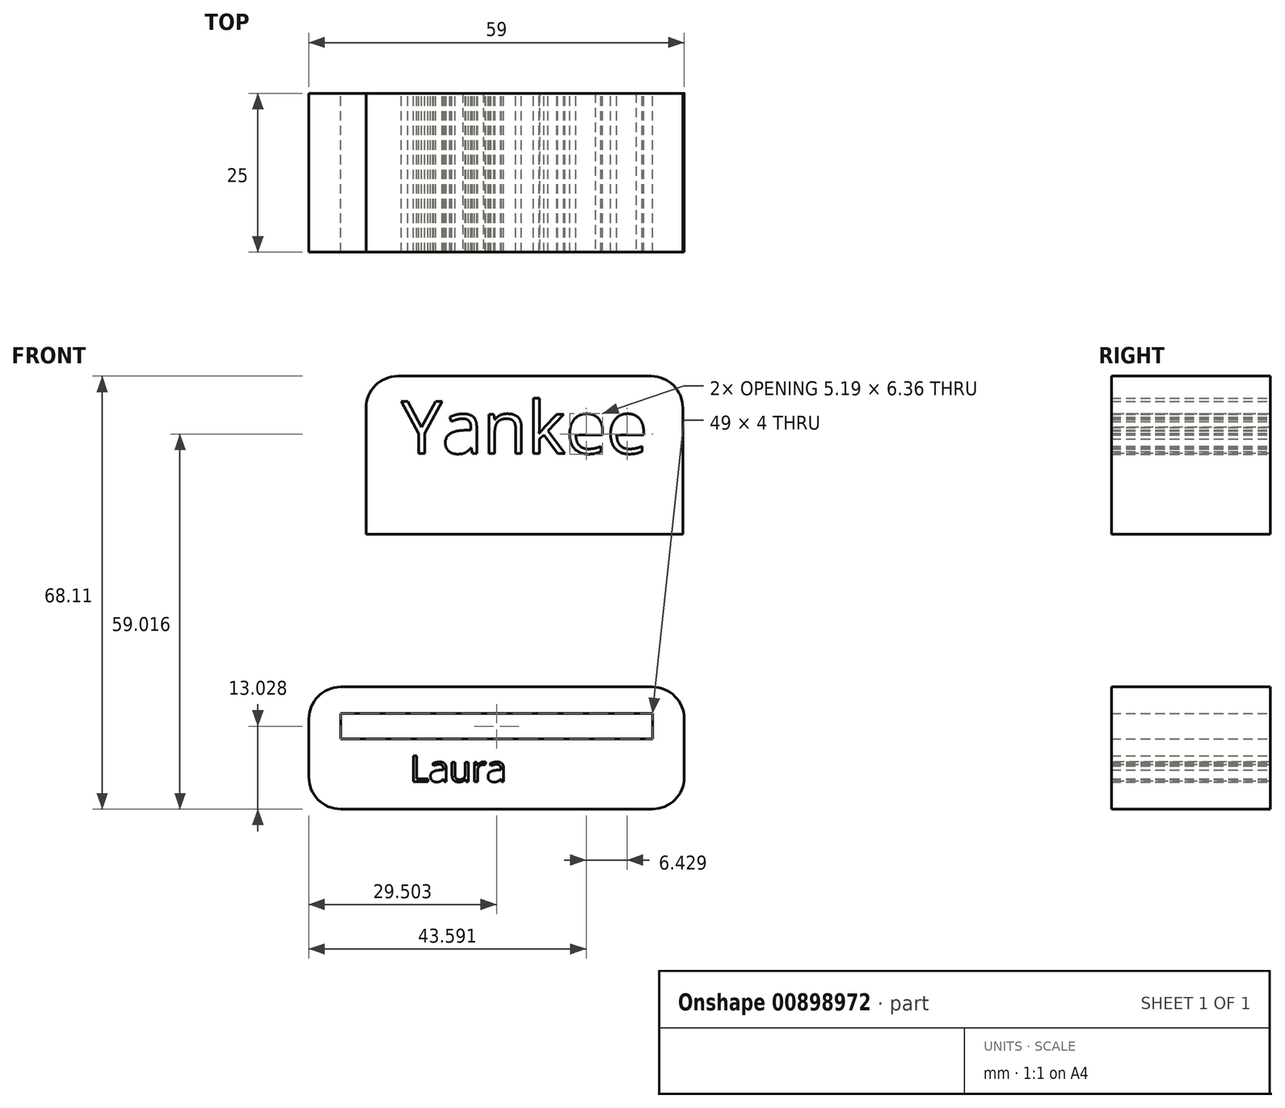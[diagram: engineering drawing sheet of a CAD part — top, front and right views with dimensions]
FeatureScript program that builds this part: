
annotation { "Feature Type Name" : "Feature", "Feature Type Description" : "" }
export const myFeature = defineFeature(function(context is Context, id is Id, definition is map)
    precondition{}
    {
        {
            var Q0;
            Q0=qCreatedBy(makeId("Front.planeOp"),FACE);
            var sketch = newSketch(context, id + "F0", { "sketchPlane" : qUnion([Q0])});
            skLineSegment(sketch, "E0.bottom", {"start": v(-11.79, -18.06) * mm, "end": v(28.01, -18.06) * mm});
            skLineSegment(sketch, "E0.top", {"start": v(-16.79, -42.95) * mm, "end": v(33.01, -42.95) * mm});
            skLineSegment(sketch, "E0.left", {"start": v(-16.79, -23.06) * mm, "end": v(-16.79, -42.95) * mm});
            skLineSegment(sketch, "E0.right", {"start": v(33.01, -23.06) * mm, "end": v(33.01, -42.95) * mm});
            skText(sketch, "E1", { "text": "Yankee\n", "fontName": "OpenSans-Regular.ttf"});
            skPoint(sketch, "E2.2.internal.snap0", {"position": v(8.11, -18.06) * mm});
            skLineSegment(sketch, "E3.bottom", {"start": v(-20.77, -86.17) * mm, "end": v(28.23, -86.17) * mm});
            skLineSegment(sketch, "E3.top", {"start": v(-20.77, -66.97) * mm, "end": v(28.23, -66.97) * mm});
            skLineSegment(sketch, "E3.left", {"start": v(-25.77, -81.17) * mm, "end": v(-25.77, -71.97) * mm});
            skLineSegment(sketch, "E3.right", {"start": v(33.23, -81.17) * mm, "end": v(33.23, -71.97) * mm});
            skPoint(sketch, "E2.2.internal.orphan", {"position": v(8.11, -10.25) * mm});
            skPoint(sketch, "E2.3.internal.orphan", {"position": v(8.16, -8.67) * mm});
            skLineSegment(sketch, "E4.bottom", {"start": v(-20.77, -71.14) * mm, "end": v(28.23, -71.14) * mm});
            skLineSegment(sketch, "E4.top", {"start": v(-20.77, -75.14) * mm, "end": v(28.23, -75.14) * mm});
            skLineSegment(sketch, "E4.left", {"start": v(-20.77, -71.14) * mm, "end": v(-20.77, -75.14) * mm});
            skLineSegment(sketch, "E4.right", {"start": v(28.23, -71.14) * mm, "end": v(28.23, -75.14) * mm});
            skPoint(sketch, "E5.visualSharp", {"position": v(-25.77, -66.97) * mm});
            skArc(sketch, "E5.filletArc", {"start": v(-20.77, -66.97) * mm, "mid": v(-24.3, -68.43) * mm, "end": v(-25.77, -71.97) * mm});
            skPoint(sketch, "E6.visualSharp", {"position": v(33.23, -66.97) * mm});
            skArc(sketch, "E6.filletArc", {"start": v(33.23, -71.97) * mm, "mid": v(31.77, -68.43) * mm, "end": v(28.23, -66.97) * mm});
            skPoint(sketch, "E7.visualSharp", {"position": v(33.23, -86.17) * mm});
            skArc(sketch, "E7.filletArc", {"start": v(28.23, -86.17) * mm, "mid": v(31.77, -84.7) * mm, "end": v(33.23, -81.17) * mm});
            skPoint(sketch, "E8.visualSharp", {"position": v(-25.77, -86.17) * mm});
            skArc(sketch, "E8.filletArc", {"start": v(-25.77, -81.17) * mm, "mid": v(-24.3, -84.7) * mm, "end": v(-20.77, -86.17) * mm});
            skPoint(sketch, "E9.visualSharp", {"position": v(33.01, -18.06) * mm});
            skArc(sketch, "E9.filletArc", {"start": v(33.01, -23.06) * mm, "mid": v(31.55, -19.53) * mm, "end": v(28.01, -18.06) * mm});
            skPoint(sketch, "E10.visualSharp", {"position": v(-16.79, -18.06) * mm});
            skArc(sketch, "E10.filletArc", {"start": v(-11.79, -18.06) * mm, "mid": v(-15.32, -19.53) * mm, "end": v(-16.79, -23.06) * mm});
            skText(sketch, "E11", { "text": "Laura\n", "fontName": "OpenSans-Regular.ttf"});
            const initialGuessF0  = {"E1": [-0.01125, -0.03022, 1, 0, 0.00825], "E11": [-0.00988, -0.08186, 1, 0, 0.00412]};
            skSetInitialGuess(sketch, initialGuessF0);
            skSolve(sketch);
        }
        {
            var Q0;
            Q0=makeQuery(id+"F0.imprint","IMPRINT",FACE,{"disambiguationData":[TD([[makeQuery(id+"F0.imprint","IMPRINT",EDGE,{"derivedFrom":sQuery(id+"F0.wireOp",EDGE,"E0.bottom")}),-1.0]])]});
            var Q1;
            Q1=makeQuery(id+"F0.imprint","IMPRINT",FACE,{"disambiguationData":[TD([[makeQuery(id+"F0.imprint","IMPRINT",EDGE,{"derivedFrom":sQuery(id+"F0.wireOp",EDGE,"E3.bottom")}),1.0]])]});
            extrude(context, id + "F1", {"entities" : qUnion([Q0, Q1]), "depth" : 25 * mm, "offsetDistance" : 25 * mm});
        }
    });
